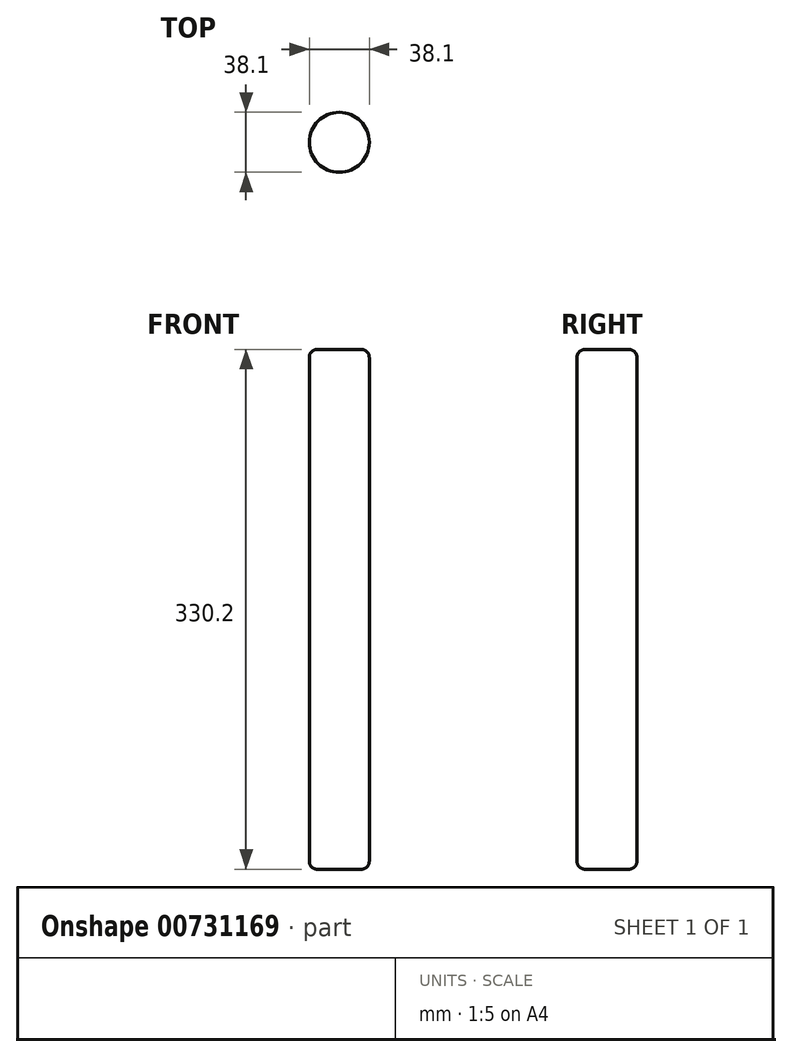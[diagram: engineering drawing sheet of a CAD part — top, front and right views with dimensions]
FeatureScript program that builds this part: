
annotation { "Feature Type Name" : "Feature", "Feature Type Description" : "" }
export const myFeature = defineFeature(function(context is Context, id is Id, definition is map)
    precondition{}
    {
        {
            var Q0;
            Q0=qCreatedBy(makeId("Top.planeOp"),FACE);
            var sketch = newSketch(context, id + "F0", { "sketchPlane" : qUnion([Q0])});
            skCircle(sketch, "E0", {"center": v(0, 0) * mm, "radius": 19.05 * mm});
            skSolve(sketch);
        }
        {
            var Q0;
            Q0 = qSketchRegion(id + "F0", true);
            extrude(context, id + "F1", {"entities" : qUnion([Q0]), "depth" : 330.2 * mm, "offsetDistance" : 25.4 * mm});
        }
        {
            var Q0;
            Q0=makeQuery(id+"F1.opExtrude","CAP_EDGE",EDGE,{"disambiguationData":[OSD([sQuery(id+"F0.wireOp",EDGE,"E0")])],"isStart":true});
            var Q1;
            Q1=makeQuery(id+"F1.opExtrude","CAP_EDGE",EDGE,{"disambiguationData":[OSD([sQuery(id+"F0.wireOp",EDGE,"E0")])],"isStart":false});
            fillet(context, id + "F2", {"entities" : qUnion([Q0, Q1]), "radius" : 5.08 * mm, "tangentPropagation" : true, "allowEdgeOverflow" : false});
        }
    });
